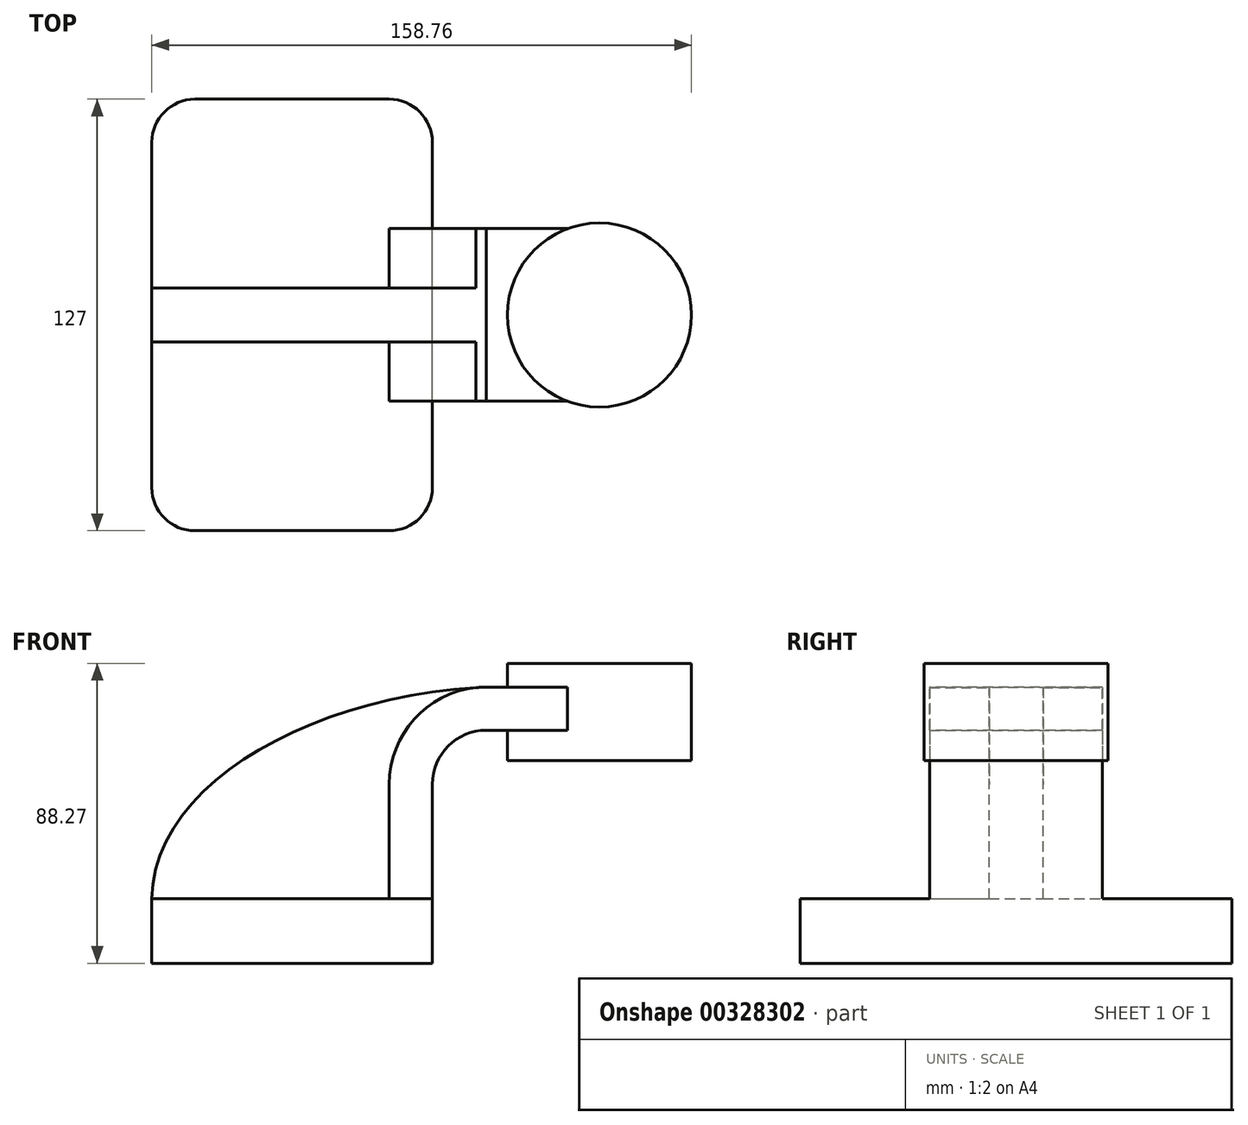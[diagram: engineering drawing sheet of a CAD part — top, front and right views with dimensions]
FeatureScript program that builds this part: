
annotation { "Feature Type Name" : "Feature", "Feature Type Description" : "" }
export const myFeature = defineFeature(function(context is Context, id is Id, definition is map)
    precondition{}
    {
        {
            var Q0;
            Q0=qCreatedBy(makeId("Front.planeOp"),FACE);
            var sketch = newSketch(context, id + "F0", { "sketchPlane" : qUnion([Q0])});
            skLineSegment(sketch, "E0.bottom", {"start": v(-41.28, -9.53) * mm, "end": v(41.28, -9.53) * mm});
            skLineSegment(sketch, "E0.top", {"start": v(-41.28, 9.53) * mm, "end": v(41.28, 9.53) * mm});
            skLineSegment(sketch, "E0.left", {"start": v(-41.28, -9.53) * mm, "end": v(-41.28, 9.53) * mm});
            skLineSegment(sketch, "E0.right", {"start": v(41.28, -9.53) * mm, "end": v(41.28, 9.53) * mm});
            skPoint(sketch, "E0.middle", {"position": v(0, 0) * mm});
            skLineSegment(sketch, "E1.bottom", {"start": v(66.68, 50.17) * mm, "end": v(117.48, 50.17) * mm});
            skLineSegment(sketch, "E1.top", {"start": v(66.68, 78.74) * mm, "end": v(117.48, 78.74) * mm});
            skLineSegment(sketch, "E1.left", {"start": v(66.68, 50.17) * mm, "end": v(66.68, 78.74) * mm});
            skLineSegment(sketch, "E1.right", {"start": v(117.48, 50.17) * mm, "end": v(117.48, 78.74) * mm});
            skPoint(sketch, "E1.middle", {"position": v(92.08, 64.45) * mm});
            skLineSegment(sketch, "E2", {"start": v(41.27, 9.52) * mm, "end": v(41.27, 43.18) * mm});
            skArc(sketch, "E3", {"start": v(41.27, 43.18) * mm, "mid": v(45.92, 54.4) * mm, "end": v(57.15, 59.06) * mm});
            skLineSegment(sketch, "E4", {"start": v(57.15, 59.06) * mm, "end": v(90.4, 59.06) * mm});
            skLineSegment(sketch, "E5.0", {"start": v(57.15, 71.76) * mm, "end": v(90.4, 71.76) * mm});
            skArc(sketch, "E5.1", {"start": v(28.57, 43.18) * mm, "mid": v(36.94, 63.39) * mm, "end": v(57.15, 71.76) * mm});
            skLineSegment(sketch, "E5.2", {"start": v(28.57, 9.52) * mm, "end": v(28.57, 43.18) * mm});
            skLineSegment(sketch, "E6", {"start": v(90.4, 59.06) * mm, "end": v(90.4, 71.76) * mm});
            skLineSegment(sketch, "E7", {"start": v(90.4, 71.76) * mm, "end": v(90.4, 78.74) * mm});
            skLineSegment(sketch, "E8", {"start": v(90.4, 78.74) * mm, "end": v(90.4, 59.06) * mm});
            skLineSegment(sketch, "E9", {"start": v(90.4, 59.06) * mm, "end": v(90.4, 50.17) * mm});
            skPoint(sketch, "E9.endSnap0", {"position": v(92.08, 50.17) * mm});
            skFitSpline(sketch, "E10", {"points": [v(-41.28, 9.52) * mm, v(57.15, 71.76) * mm], "startDerivative": vector(1.5, 102.47) * mm, "endDerivative": vector(151.7, 6.83) * mm});
            skSolve(sketch);
        }
        {
            var Q0;
            Q0=makeQuery(id+"F0.imprint","IMPRINT",FACE,{"disambiguationData":[TD([[makeQuery(id+"F0.imprint","IMPRINT",EDGE,{"derivedFrom":sQuery(id+"F0.wireOp",EDGE,"E0.bottom")}),1.0]])]});
            extrude(context, id + "F1", {"entities" : qUnion([Q0]), "endBound" : BoundingType.SYMMETRIC, "depth" : 127 * mm});
        }
        {
            var Q0;
            {var subQ0=sQuery(id+"F0.wireOp",EDGE,"E4");var subQ1=sQuery(id+"F0.wireOp",EDGE,"E1.left");var subQ2=makeQuery(id+"F0.imprint","INTERSECT",VERTEX,{"derivedFrom":[subQ1,subQ0]});Q0=makeQuery(id+"F0.imprint","IMPRINT",FACE,{"disambiguationData":[TD([[makeQuery(id+"F0.imprint","IMPRINT",EDGE,{"disambiguationData":[TD([[subQ2,-1.0]])],"derivedFrom":subQ1}),-1.0]])]});}
            var Q1;
            {var subQ1=sQuery(id+"F0.wireOp",EDGE,"E2");Q1=makeQuery(id+"F0.imprint","IMPRINT",FACE,{"disambiguationData":[TD([[makeQuery(id+"F0.imprint","IMPRINT",EDGE,{"derivedFrom":subQ1}),1.0]])]});}
            extrude(context, id + "F2", {"entities" : qUnion([Q0, Q1]), "operationType" : NewBodyOperationType.ADD, "endBound" : BoundingType.SYMMETRIC, "depth" : 50.8 * mm});
        }
        {
            var Q0;
            {var subQ3=sQuery(id+"F0.wireOp",EDGE,"E5.2");Q0=makeQuery(id+"F0.imprint","IMPRINT",FACE,{"disambiguationData":[TD([[makeQuery(id+"F0.imprint","IMPRINT",EDGE,{"derivedFrom":subQ3}),1.0]])]});}
            extrude(context, id + "F3", {"entities" : qUnion([Q0]), "operationType" : NewBodyOperationType.ADD, "endBound" : BoundingType.SYMMETRIC, "depth" : 15.88 * mm});
        }
        {
            var Q0;
            {var subQ4=sQuery(id+"F0.wireOp",EDGE,"E1.right");Q0=makeQuery(id+"F0.imprint","IMPRINT",FACE,{"disambiguationData":[TD([[makeQuery(id+"F0.imprint","IMPRINT",EDGE,{"derivedFrom":subQ4}),1.0]])]});}
            var Q1;
            Q1=sQuery(id+"F0.wireOp",EDGE,"E8");
            revolve(context, id + "F4", {"operationType" : NewBodyOperationType.ADD, "entities" : qUnion([Q0]), "axis" : qUnion([Q1]), "revolveType" : RevolveType.FULL});
        }
        {
            var Q0;
            Q0=makeQuery(id+"F1.opExtrude","CAP_EDGE",EDGE,{"disambiguationData":[OSD([sQuery(id+"F0.wireOp",EDGE,"E0.right")])],"isStart":false});
            var Q1;
            Q1=makeQuery(id+"F1.opExtrude","CAP_EDGE",EDGE,{"disambiguationData":[OSD([sQuery(id+"F0.wireOp",EDGE,"E0.left")])],"isStart":false});
            var Q2;
            Q2=makeQuery(id+"F1.opExtrude","CAP_EDGE",EDGE,{"disambiguationData":[OSD([sQuery(id+"F0.wireOp",EDGE,"E0.left")])],"isStart":true});
            var Q3;
            Q3=makeQuery(id+"F1.opExtrude","CAP_EDGE",EDGE,{"disambiguationData":[OSD([sQuery(id+"F0.wireOp",EDGE,"E0.right")])],"isStart":true});
            fillet(context, id + "F5", {"entities" : qUnion([Q0, Q1, Q2, Q3]), "radius" : 12.7 * mm, "tangentPropagation" : true, "allowEdgeOverflow" : false});
        }
    });
